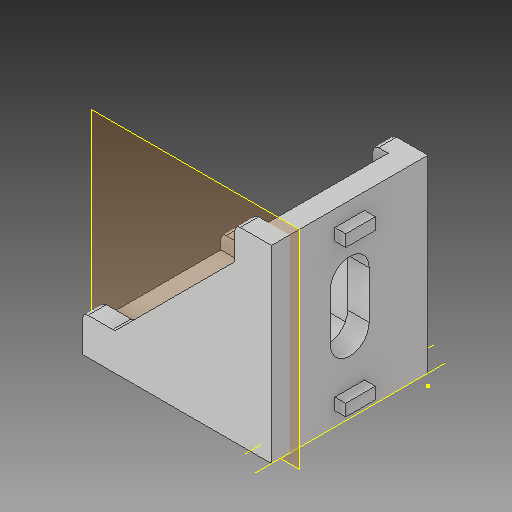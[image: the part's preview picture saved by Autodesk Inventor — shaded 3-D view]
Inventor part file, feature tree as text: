
AUTODESK INVENTOR PART (.ipt)
format: ipt  version: 2017 (Build 210142000, 142)  size: 223,232 bytes
history: native  units: mm
features: sketch x7, extrude x5, other x2, plane x1, fillet x1, pattern_circular x1, projected_geometry x1
ambient origin geometry x8: Origin, YZ Plane, XZ Plane, XY Plane, X Axis, Y Axis, Z Axis, Center Point
bodies: Solid1 (feature_tree)
feature tree (18):
  extrude  "Extrusion1"  Depth=6.8mm
  plane  "Work Plane1"
  extrude  "Extrusion2"  Depth=6.0mm
  extrude  "Extrusion3"  TaperAngle=180.0deg  [1 undecoded]
  fillet  "Fillet1"  Radius=6.8mm
  sketch  "Sketch4"  dims[d7=6.0mm]
  other  "Work Axis1"
  pattern_circular  "Circular Pattern1"  [2 undecoded]
  extrude  "Extrusion4"  Depth=4.0mm
  other  "Work Axis2"
  sketch  "Sketch7"  dims[d9=1.0mm]
  extrude  "Extrusion5"  Depth=22.2mm TaperAngle=0.0deg
  sketch  "Sketch1"  dims[d0=35.0mm d1=6.8mm]
  sketch  "Sketch2"  dims[d2=90.0deg d3=6.0mm]
  sketch  "Sketch3"  dims[d4=35.0mm d5=180.0deg d6=6.8mm]
  sketch  "Sketch5"  dims[d8=90.0deg]
  sketch  "Sketch9"  dims[d10=29.0mm d11=0.0mm d12=-3.4mm d13=4.0mm d14=22.2mm d15=0.0mm d16=9.0mm d17=3.6mm d18=16.0mm d19=3.6mm d20=22.2mm d21=0.0mm d22=1.0mm d23=2.0mm d24=2.0mm d25=2.0mm d26=20.0mm d27=270.0deg d29=3.0mm d30=0.0mm d31=2.75mm d32=5.5mm d33=2.2mm d34=2.6mm d35=2.75mm d36=2.2mm d37=5.5mm d38=2.0mm d39=0.0mm d41=2.0mm d42=0.0mm]
  projected_geometry  "Projected Loop4"
note: 3 required parameter values undecoded (feature->parameter linkage not recoverable at this tier; creation-order binding heuristic only, values carry confidence <= 0.55)
